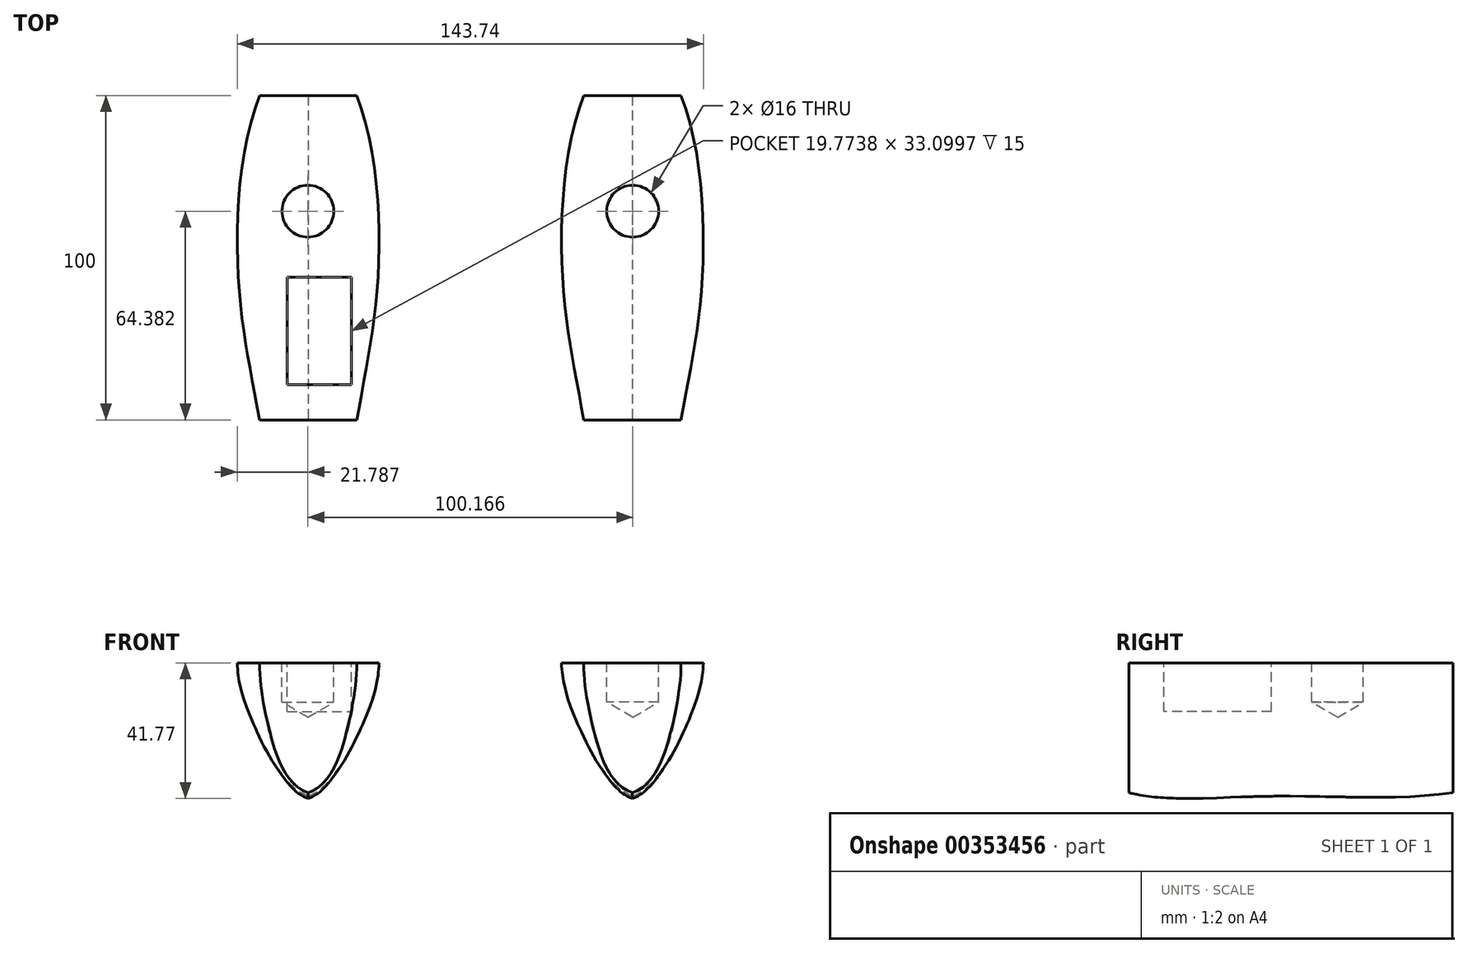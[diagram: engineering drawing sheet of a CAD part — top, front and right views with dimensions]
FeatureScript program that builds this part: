
annotation { "Feature Type Name" : "Feature", "Feature Type Description" : "" }
export const myFeature = defineFeature(function(context is Context, id is Id, definition is map)
    precondition{}
    {
        {
            var Q0;
            Q0=qCreatedBy(makeId("Front.planeOp"),FACE);
            cPlane(context, id + "F0", {"entities" : qUnion([Q0]), "cplaneType" : CPlaneType.OFFSET, "offset" : 100 * mm, "width" : 150 * mm, "height" : 150 * mm});
        }
        {
            var Q0;
            Q0=qCreatedBy(makeId("Right.planeOp"),FACE);
            cPlane(context, id + "F1", {"entities" : qUnion([Q0]), "cplaneType" : CPlaneType.OFFSET, "offset" : 50 * mm, "width" : 150 * mm, "height" : 150 * mm});
        }
        {
            var Q0;
            Q0=qCreatedBy(makeId("Front.planeOp"),FACE);
            var sketch = newSketch(context, id + "F2", { "sketchPlane" : qUnion([Q0])});
            skFitSpline(sketch, "E0", {"points": [v(35, 0) * mm, v(38, -21.77) * mm, v(50, -40) * mm], "startDerivative": vector(2.25, -47.82) * mm, "endDerivative": vector(42.21, -20.3) * mm});
            skLineSegment(sketch, "E1", {"start": v(35, 0) * mm, "end": v(50, 0) * mm});
            skLineSegment(sketch, "E2", {"start": v(50, 0) * mm, "end": v(50, -40) * mm});
            skSolve(sketch);
        }
        {
            var Q0;
            Q0=qCreatedBy(id+"F0.planeOp",FACE);
            var sketch = newSketch(context, id + "F3", { "sketchPlane" : qUnion([Q0])});
            skFitSpline(sketch, "E3", {"points": [v(35, 0) * mm, v(38, -20.54) * mm, v(50, -40) * mm], "startDerivative": vector(0.25, -39.17) * mm, "endDerivative": vector(41.15, -12.9) * mm});
            skLineSegment(sketch, "E4", {"start": v(35, 0) * mm, "end": v(50, 0) * mm});
            skLineSegment(sketch, "E5", {"start": v(50, 0) * mm, "end": v(50, -40) * mm});
            skSolve(sketch);
        }
        {
            var Q0;
            Q0=qCreatedBy(id+"F1.planeOp",FACE);
            var sketch = newSketch(context, id + "F4", { "sketchPlane" : qUnion([Q0])});
            skFitSpline(sketch, "E6", {"points": [v(0, -40) * mm, v(-55.86, -41.07) * mm, v(-100, -40) * mm], "startDerivative": vector(-97.87, -14.48) * mm, "endDerivative": vector(-77.43, 19.4) * mm});
            skSolve(sketch);
        }
        {
            var Q0;
            Q0=qCreatedBy(makeId("Top.planeOp"),FACE);
            var sketch = newSketch(context, id + "F5", { "sketchPlane" : qUnion([Q0])});
            skFitSpline(sketch, "E7", {"points": [v(35, 0) * mm, v(28.54, -57.47) * mm, v(35, -100) * mm], "startDerivative": vector(-36.01, -91.38) * mm, "endDerivative": vector(16.6, -94.55) * mm});
            skSolve(sketch);
        }
        {
            var Q0;
            Q0=makeQuery(id+"F3.imprint","IMPRINT",FACE,{"disambiguationData":[TD([[makeQuery(id+"F3.imprint","IMPRINT",EDGE,{"derivedFrom":sQuery(id+"F3.wireOp",EDGE,"E3")}),1.0]])]});
            var Q1;
            Q1=makeQuery(id+"F2.imprint","IMPRINT",FACE,{"disambiguationData":[TD([[makeQuery(id+"F2.imprint","IMPRINT",EDGE,{"derivedFrom":sQuery(id+"F2.wireOp",EDGE,"E0")}),1.0]])]});
            var Q2;
            Q2=sQuery(id+"F5.wireOp",EDGE,"E7");
            var Q3;
            Q3=sQuery(id+"F4.wireOp",EDGE,"E6");
            loft(context, id + "F6", {"addGuides" : true, "sheetProfilesArray" : [{ "sheetProfileEntities" : qUnion([Q0]) }, { "sheetProfileEntities" : qUnion([Q1]) }], "guidesArray" : [{ "guideEntities" : qUnion([Q2]), "guideDerivativeType" : LoftGuideDerivativeType.DEFAULT, "guideDerivativeMagnitude" : 1 }, { "guideEntities" : qUnion([Q3]), "guideDerivativeType" : LoftGuideDerivativeType.DEFAULT, "guideDerivativeMagnitude" : 1 }]});
        }
        {
            var Q0;
            Q0=makeQuery(id+"F6.opLoft","SWEPT_BODY",BODY,{"disambiguationData":[OSD([makeQuery(id+"F2.imprint","IMPRINT",FACE,{"disambiguationData":[TD([[makeQuery(id+"F2.imprint","IMPRINT",EDGE,{"derivedFrom":sQuery(id+"F2.wireOp",EDGE,"E0")}),1.0]])]}),makeQuery(id+"F3.imprint","IMPRINT",FACE,{"disambiguationData":[TD([[makeQuery(id+"F3.imprint","IMPRINT",EDGE,{"derivedFrom":sQuery(id+"F3.wireOp",EDGE,"E3")}),1.0]])]}),sQuery(id+"F4.wireOp",EDGE,"E6"),sQuery(id+"F5.wireOp",EDGE,"E7")])]});
            var Q1;
            Q1=qCreatedBy(id+"F1.planeOp",FACE);
            mirror(context, id + "F7", {"operationType" : NewBodyOperationType.ADD, "entities" : qUnion([Q0]), "mirrorPlane" : qUnion([Q1])});
        }
        {
            var Q0;
            Q0=makeQuery(id+"F6.opLoft","SWEPT_BODY",BODY,{"disambiguationData":[OSD([makeQuery(id+"F2.imprint","IMPRINT",FACE,{"disambiguationData":[TD([[makeQuery(id+"F2.imprint","IMPRINT",EDGE,{"derivedFrom":sQuery(id+"F2.wireOp",EDGE,"E0")}),1.0]])]}),makeQuery(id+"F3.imprint","IMPRINT",FACE,{"disambiguationData":[TD([[makeQuery(id+"F3.imprint","IMPRINT",EDGE,{"derivedFrom":sQuery(id+"F3.wireOp",EDGE,"E3")}),1.0]])]}),sQuery(id+"F4.wireOp",EDGE,"E6"),sQuery(id+"F5.wireOp",EDGE,"E7")])]});
            var Q1;
            Q1=qCreatedBy(makeId("Right.planeOp"),FACE);
            mirror(context, id + "F8", {"entities" : qUnion([Q0]), "mirrorPlane" : qUnion([Q1])});
        }
        {
            var Q0;
            {var subQ0=makeQuery(id+"F6.opLoft","SWEPT_FACE",FACE,{"disambiguationData":[OSD([sQuery(id+"F2.wireOp",EDGE,"E1"),sQuery(id+"F2.wireOp",EDGE,"E2"),sQuery(id+"F3.wireOp",EDGE,"E4"),sQuery(id+"F3.wireOp",EDGE,"E5"),sQuery(id+"F5.wireOp",EDGE,"E7")])]});Q0=makeQuery(id+"F7.boolean.opBoolean","MERGE",FACE,{"derivedFrom":[subQ0,makeQuery(id+"F7.opPattern","COPY",FACE,{"derivedFrom":subQ0,"instanceName":"1"})]});}
            var sketch = newSketch(context, id + "F9", { "sketchPlane" : qUnion([Q0])});
            skCircle(sketch, "E8", {"center": v(50.08, -35.62) * mm, "radius": 8.53 * mm});
            skSolve(sketch);
        }
        {
            var Q0;
            Q0=sQuery(id+"F9.wireOp",VERTEX,"E8.center");
            var Q1;
            Q1=makeQuery(id+"F6.opLoft","SWEPT_BODY",BODY,{"disambiguationData":[OSD([makeQuery(id+"F2.imprint","IMPRINT",FACE,{"disambiguationData":[TD([[makeQuery(id+"F2.imprint","IMPRINT",EDGE,{"derivedFrom":sQuery(id+"F2.wireOp",EDGE,"E0")}),1.0]])]}),makeQuery(id+"F3.imprint","IMPRINT",FACE,{"disambiguationData":[TD([[makeQuery(id+"F3.imprint","IMPRINT",EDGE,{"derivedFrom":sQuery(id+"F3.wireOp",EDGE,"E3")}),1.0]])]}),sQuery(id+"F4.wireOp",EDGE,"E6"),sQuery(id+"F5.wireOp",EDGE,"E7")])]});
            hole(context, id + "F10", {"style" : HoleStyle.SIMPLE, "endStyle" : HoleEndStyle.BLIND, "holeDiameter" : 16 * mm, "holeDepth" : 12 * mm, "isTappedThrough" : true, "tappedDepth" : 12 * mm, "tapClearance" : 3, "locations" : qUnion([Q0]), "scope" : qUnion([Q1])});
        }
        {
            var Q0;
            Q0=makeQuery(id+"F8.opPattern","COPY",BODY,{"derivedFrom":makeQuery(id+"F6.opLoft","SWEPT_BODY",BODY,{"disambiguationData":[OSD([makeQuery(id+"F2.imprint","IMPRINT",FACE,{"disambiguationData":[TD([[makeQuery(id+"F2.imprint","IMPRINT",EDGE,{"derivedFrom":sQuery(id+"F2.wireOp",EDGE,"E0")}),1.0]])]}),makeQuery(id+"F3.imprint","IMPRINT",FACE,{"disambiguationData":[TD([[makeQuery(id+"F3.imprint","IMPRINT",EDGE,{"derivedFrom":sQuery(id+"F3.wireOp",EDGE,"E3")}),1.0]])]}),sQuery(id+"F4.wireOp",EDGE,"E6"),sQuery(id+"F5.wireOp",EDGE,"E7")])]}),"instanceName":"1"});
            deleteBodies(context, id + "F11", {"entities" : qUnion([Q0])});
        }
        {
            var Q0;
            Q0=makeQuery(id+"F6.opLoft","SWEPT_BODY",BODY,{"disambiguationData":[OSD([makeQuery(id+"F2.imprint","IMPRINT",FACE,{"disambiguationData":[TD([[makeQuery(id+"F2.imprint","IMPRINT",EDGE,{"derivedFrom":sQuery(id+"F2.wireOp",EDGE,"E0")}),1.0]])]}),makeQuery(id+"F3.imprint","IMPRINT",FACE,{"disambiguationData":[TD([[makeQuery(id+"F3.imprint","IMPRINT",EDGE,{"derivedFrom":sQuery(id+"F3.wireOp",EDGE,"E3")}),1.0]])]}),sQuery(id+"F4.wireOp",EDGE,"E6"),sQuery(id+"F5.wireOp",EDGE,"E7")])]});
            var Q1;
            Q1=qCreatedBy(makeId("Right.planeOp"),FACE);
            mirror(context, id + "F12", {"entities" : qUnion([Q0]), "mirrorPlane" : qUnion([Q1])});
        }
        {
            var Q0;
            {var subQ0=makeQuery(id+"F6.opLoft","SWEPT_FACE",FACE,{"disambiguationData":[OSD([sQuery(id+"F2.wireOp",EDGE,"E1"),sQuery(id+"F2.wireOp",EDGE,"E2"),sQuery(id+"F3.wireOp",EDGE,"E4"),sQuery(id+"F3.wireOp",EDGE,"E5"),sQuery(id+"F5.wireOp",EDGE,"E7")])]});Q0=makeQuery(id+"F12.opPattern","COPY",FACE,{"derivedFrom":makeQuery(id+"F7.boolean.opBoolean","MERGE",FACE,{"derivedFrom":[subQ0,makeQuery(id+"F7.opPattern","COPY",FACE,{"derivedFrom":subQ0,"instanceName":"1"})]}),"instanceName":"1"});}
            var sketch = newSketch(context, id + "F13", { "sketchPlane" : qUnion([Q0])});
            skLineSegment(sketch, "E9.bottom", {"start": v(-56.45, -56.02) * mm, "end": v(-36.68, -56.02) * mm});
            skLineSegment(sketch, "E9.top", {"start": v(-56.45, -89.12) * mm, "end": v(-36.68, -89.12) * mm});
            skLineSegment(sketch, "E9.left", {"start": v(-56.45, -56.02) * mm, "end": v(-56.45, -89.12) * mm});
            skLineSegment(sketch, "E9.right", {"start": v(-36.68, -56.02) * mm, "end": v(-36.68, -89.12) * mm});
            skSolve(sketch);
        }
        {
            var Q0;
            Q0=makeQuery(id+"F13.imprint","IMPRINT",FACE,{"disambiguationData":[TD([[makeQuery(id+"F13.imprint","IMPRINT",EDGE,{"derivedFrom":sQuery(id+"F13.wireOp",EDGE,"E9.bottom")}),-1.0]])]});
            extrude(context, id + "F14", {"entities" : qUnion([Q0]), "operationType" : NewBodyOperationType.REMOVE, "oppositeDirection" : true, "depth" : 15 * mm});
        }
    });
